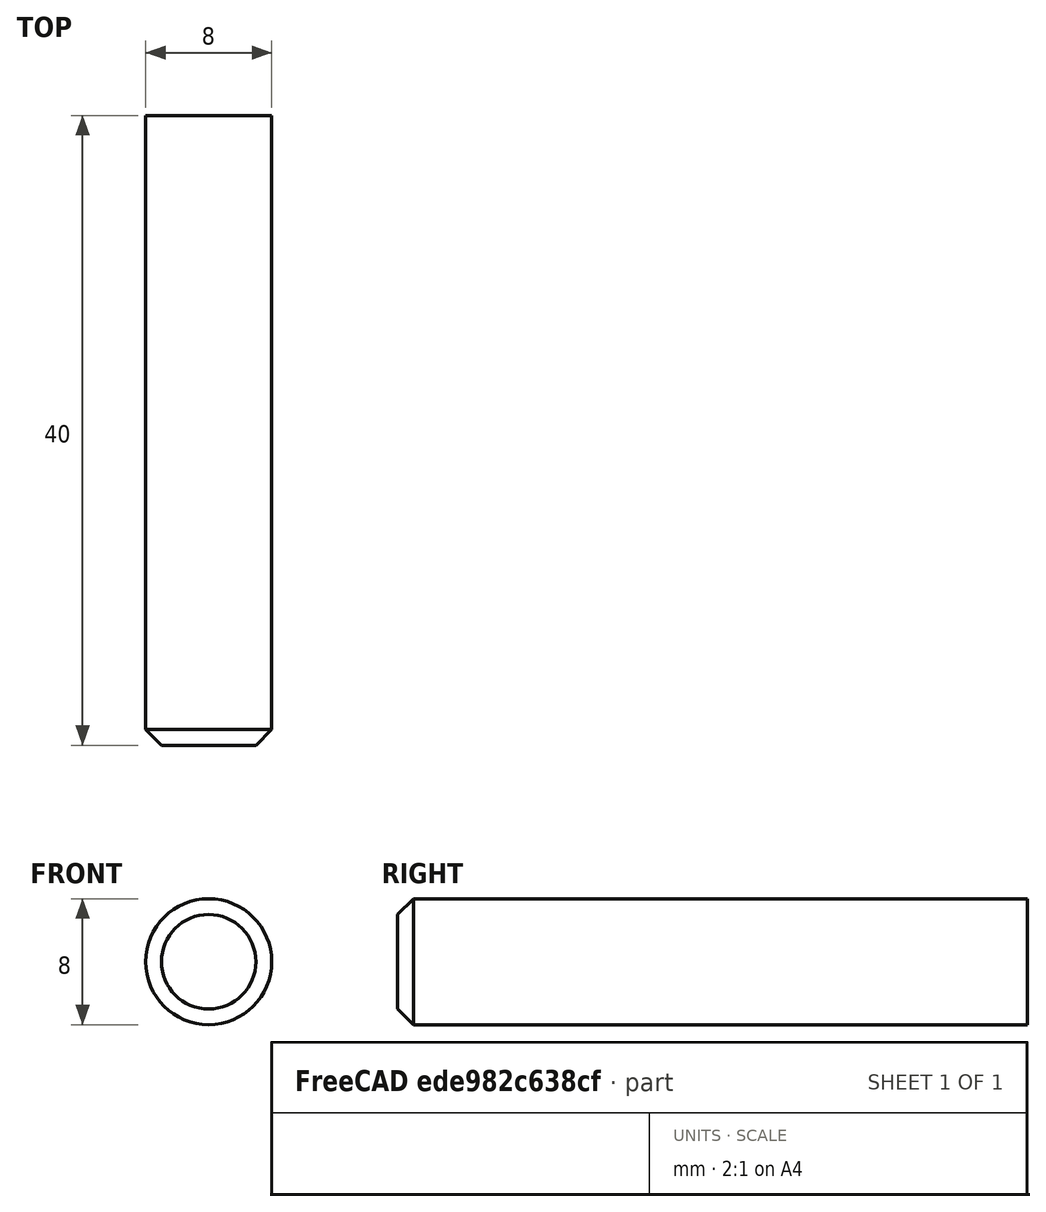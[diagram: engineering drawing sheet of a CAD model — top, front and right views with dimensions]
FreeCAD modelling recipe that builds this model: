
FCSTD DOCUMENT  (FreeCAD 0.18R4 (GitTag))
Label: EjeMotor
License: All rights reserved
LicenseURL: http://en.wikipedia.org/wiki/All_rights_reserved
objects: Sketcher::SketchObject×1, PartDesign::Pad×1, PartDesign::Chamfer×1, PartDesign::Body×1
note: 5 computed .brp shape members not serialized (recipe doc carries the construction recipe); baked Part::Feature solids carry a one-line shape summary decoded from their .brp

FEATURE [Sketcher::SketchObject] Sketch
  MapMode = 5
  Placement = pos=(0,0,0) rot=(1,0,0;1.5708rad)
  Support = -> [XZ_Plane]
  sketch-geometry (1):
    g0: Circle CenterX=0 CenterY=0 CenterZ=0 NormalX=0 NormalY=0 NormalZ=1 AngleXU=0 Radius=4
  constraints (1):
    c: Radius(g0) = 4
FEATURE [PartDesign::Pad] Pad
  Length = 40
  Length2 = 100
  Placement = pos=(0,0,0) rot=(1,0,0;1.5708rad)
  Profile = -> Sketch
  Type = 0
FEATURE [PartDesign::Chamfer] Chamfer
  Base = -> Pad [Edge3]
  BaseFeature = -> Pad
  Placement = pos=(0,0,0) rot=(1,0,0;1.5708rad)
  Size = 1
FEATURE [PartDesign::Body] Body
  Group = -> [Sketch,Pad,Chamfer]
  Origin = -> Origin
  Tip = -> Chamfer
